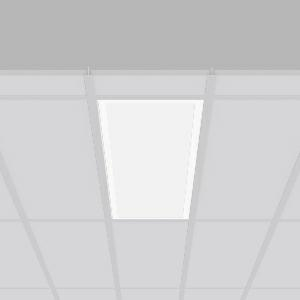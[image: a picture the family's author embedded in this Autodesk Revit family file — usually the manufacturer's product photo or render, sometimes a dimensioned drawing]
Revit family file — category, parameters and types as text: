
# Revit family: sidelite_eco_672377_002_1_04_fdd6
name_source: partatom
category: Lighting Fixtures
units: mm (PartAtom-declared; Revit-internal decimal feet)

## family parameters
Cut with Voids When Loaded = No
Host = Face
Light Source = No
Part Type = Normal
Room Calculation Point = No
Round Connector Dimension = Use Diameter
Shared = No

## types (1)
- SIDELITE ECO (1 x LED Modul 840, 3500 lm, 4000)
    Apparent Load = 29 VA
    CIE Flux Codes = 47 79 96 100 100
    Color Rendering = 80
    Color Temperature = 4000
    Default Elevation = 1800 mm
    Description = Series: SIDELITE ECO
Highly economical recessed luminaire with progressive LED technology. For escape route illumination. Frame made of aluminium, powder-coated. Diffuser: plastic, opal. Lightguide and diffuser made of non-yellowing plastic (PMMA). Lateral light emission (RZB SIDELITE technology) for homogeneous light distribution. External driver. Self-contained system with automatic self-test and feedback to the RZB monitoring system MULTIDIGIT. External driver with simple plug-in locking system. Extended connection cable (1.90 m). 
Colour: white
Length: 1245 mm
Width: 308 mm
Cut-out length: 1220 mm
Cut-out width: 285 mm
Recess height: 160 mm
Luminaire: recess height: 40 mm
Weight: 4.7 kg
Operating mode: maintained power mode
Duration time: 3 h
Lamp: LED
Socket: without socket
Colour temperature: 4000K
Colour rendering index (CRI): 80
System power: 29 W
Rated luminous flux: 3500 lm
Luminous flux, emergency: 520 lm
System power, emergency: -
Control gear: Regulated power supply
Protection class: I
Type of protection: IP 40
    Height = 0 mm  [stored 0 ft]
    Lamp = 1 x LED Modul 840
    Lamp Light Flux = 3500 lm
    Lamp count = 1
    Length = 1245 mm
    Lifetime = 50000 h
    Luminous efficacy = 121 lm/W
    Manufacturer = RZB
    ModVariant = No
    Model = 672377.002.1.04
    Mounting Place = Ceiling
    Mounting Type = Recessed
    Number of Poles = 1
    OnlyDefault = Yes
    Power Factor = 1
    Product Name = SIDELITE ECO
    Product group = Recessed modular luminaires
    ProductGroupID = 406
    Protection Class = Protection class I
    Protection Degree = IP 40
    RLX_Detail_Level = 1
    RLX_Emergency_Light_Flux = 520 lm
    RLX_Emergency_Type = 3
    RLX_Emergency_Type_DB = Yes
    RlxData = <blob elided: 30029 chars, md5=10c1cee4>
    Socket = socket
    Standby Power = 0 W
    System Light Flux = 3500 lm
    System Power = 29 W
    Type Comments = Product without accessories
    Type Image = 312367.002.jpg
    URL = http://relux.com
    VarID = ---
    Voltage = 230 V
    Voltage Range = 220-240 V
    Weight = 0.00 kg
    Width = 308 mm

note: [stored X ft] marks values corroborated as IEEE doubles in the binary element streams (Revit-internal decimal feet)

## geometry (parser evidence)
native form markers: Blend x4, Sweep x12
no freeform markers — native parametric forms only
